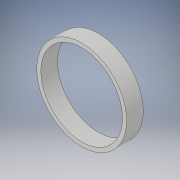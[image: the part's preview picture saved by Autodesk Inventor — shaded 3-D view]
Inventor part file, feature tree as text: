
AUTODESK INVENTOR PART (.ipt)
format: ipt  version: 2019 (Build 230136000, 136)  size: 104,960 bytes
history: native  units: mm
features: extrude x2, sketch x2
ambient origin geometry x8: Origin, YZ Plane, XZ Plane, XY Plane, X Axis, Y Axis, Z Axis, Center Point
bodies: Solid1 (feature_tree)
feature tree (4):
  extrude  "Extrusion1"  Depth=1.74mm TaperAngle=0.0deg
  extrude  "Extrusion2"  Depth=1.74mm TaperAngle=0.0deg
  sketch  "Sketch1"  dims[d0=9.42mm d1=1.74mm d2=0.0mm]
  sketch  "Sketch2"  dims[d3=8.56mm d4=1.74mm d5=0.0mm]
